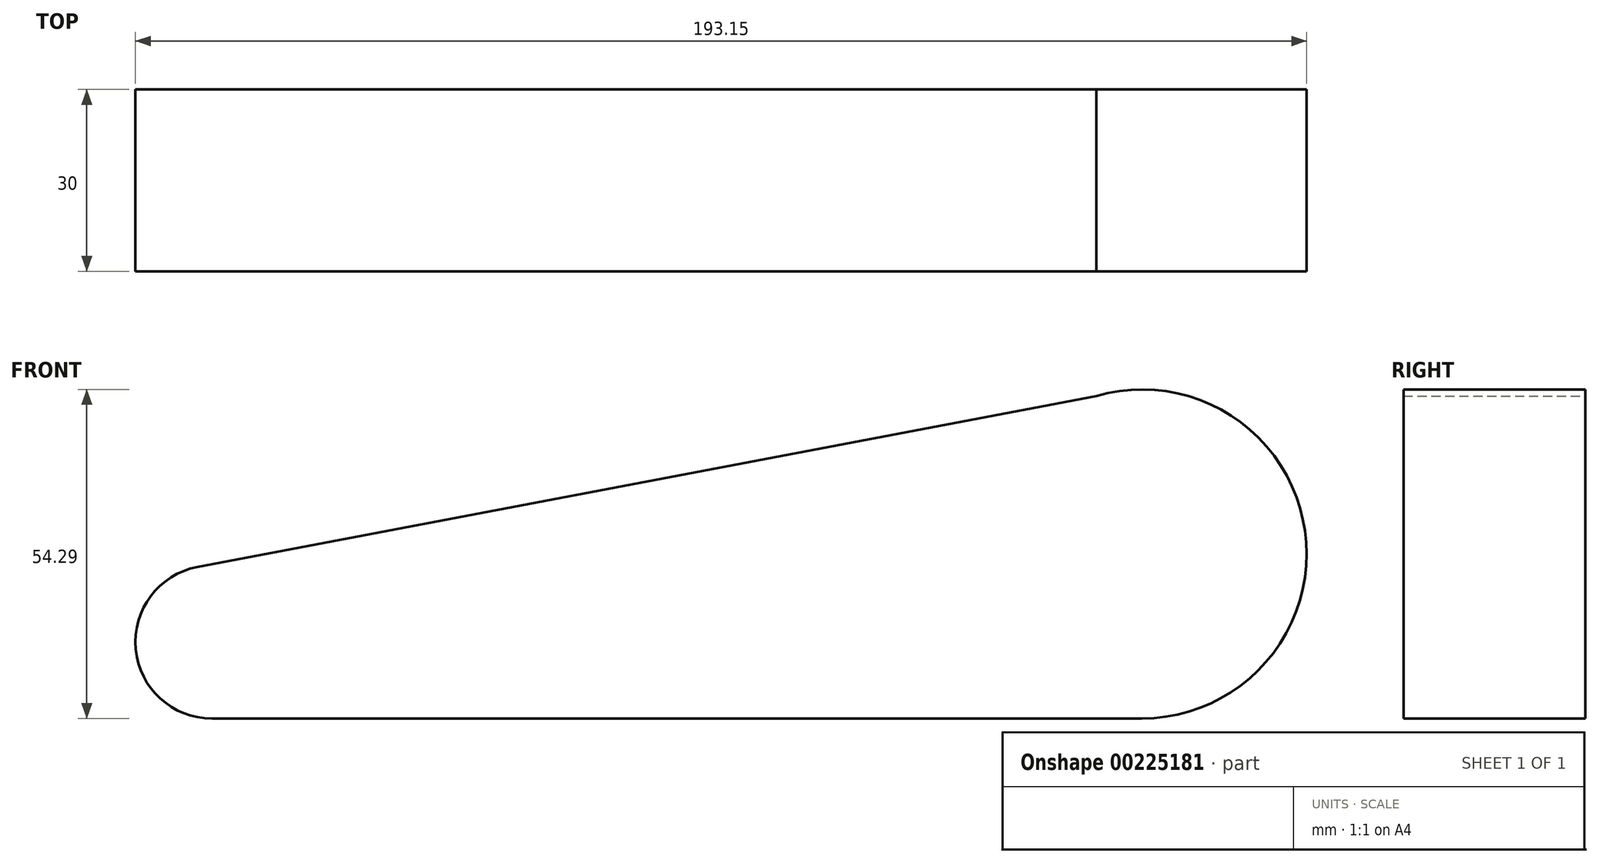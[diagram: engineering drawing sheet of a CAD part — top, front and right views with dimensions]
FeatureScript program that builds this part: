
annotation { "Feature Type Name" : "Feature", "Feature Type Description" : "" }
export const myFeature = defineFeature(function(context is Context, id is Id, definition is map)
    precondition{}
    {
        {
            var Q0;
            Q0=qCreatedBy(makeId("Front.planeOp"),FACE);
            var sketch = newSketch(context, id + "F0", { "sketchPlane" : qUnion([Q0])});
            skCircle(sketch, "E0", {"center": v(-94.73, 24.24) * mm, "radius": 12.61 * mm});
            skCircle(sketch, "E1", {"center": v(58.67, 38.78) * mm, "radius": 27.15 * mm});
            skLineSegment(sketch, "E2", {"start": v(-97.1, 36.63) * mm, "end": v(51.12, 64.85) * mm});
            skLineSegment(sketch, "E3", {"start": v(-94.73, 11.63) * mm, "end": v(58.67, 11.63) * mm});
            skSolve(sketch);
        }
        {
            var Q0;
            Q0 = qSketchRegion(id + "F0", true);
            extrude(context, id + "F1", {"entities" : qUnion([Q0]), "depth" : 30 * mm});
        }
    });
